# Revit family: toledo_flatliner_901631_002_76_a09a
name_source: partatom
category: Lighting Fixtures
units: mm (PartAtom-declared; Revit-internal decimal feet)

## family parameters
Cut with Voids When Loaded = No
Host = Face
Light Source = No
Part Type = Normal
Room Calculation Point = No
Round Connector Dimension = Use Diameter
Shared = No

## types (1)
- 982300.002 (1 x LED Modul 830, 610 lm, 3000)
    Apparent Load = 8 VA
    CIE Flux Codes = 56 78 92 81 100
    Color Rendering = 80
    Color Temperature = 3000
    Default Elevation = 1800 mm
    Description = Series: TOLEDO FLATLINER
Decorative pendant luminaire for interior decoration. Base luminaire prepared for the installation of fabric lampshade. Cylinder housing sheet steel, powder-coated. Housing: die cast aluminium and sheet steel, powder-coated. Bezel ring: die-cast aluminium, powder-coated. Canopy: sheet steel, powder-coated. Lightguide and diffuser made of non-yellowing plastic (PMMA) opal matt. Transparent suspension cable 2 m, can be shortened. Modular design: With the basic luminaire, a square or cylindrical fabric lampshade must always be ordered separately. Fabric lampshades can be fitted to the basic luminaire without tools. Order satin finish diffuser as separate accessory. 
Colour: white
Diameter: 204 mm
Height: 90.5 mm
Suspension length: 2000 mm
Lamp: LED
Socket: without socket
Colour temperature: 3000K
Colour rendering index (CRI): 80
System power: 7.7 W
Rated luminous flux: 610 lm
Luminous efficiency: 79 lm/W
Control gear: Converter, dimmable, DALI
Protection class: I
Type of protection: IP 20
    Height = 91 mm
    Lamp = 1 x LED Modul 830
    Lamp Light Flux = 610 lm
    Lamp count = 1
    Length = 204 mm
    Lifetime = 50000 h
    Luminous efficacy = 79 lm/W
    Manufacturer = RZB
    ModVariant = No
    Model = 901631.002.76
    Mounting Place = Ceiling
    Mounting Type = Pendant
    Number of Poles = 1
    OnlyDefault = Yes
    Power Factor = 1
    Product Name = TOLEDO FLATLINER
    Product group = Pendant-Fabric lampshade luminaires
    ProductGroupID = 913
    Protection Class = Protection class I
    Protection Degree = IP 20
    RLX_Detail_Level = 1
    RLX_Emergency_Light_Flux = 0 lm
    RLX_Emergency_Type = 0
    RLX_Emergency_Type_DB = No
    RlxData = <blob elided: 48449 chars, md5=f884ae04>
    Socket = socket
    Standby Power = 0 W
    System Light Flux = 610 lm
    System Power = 8 W
    Type Image = toledo_flatliner_pendel_runde_grun_odeckel.jpg
    URL = http://relux.com
    VarID = 982300_002_5a54
    Voltage = 230 V
    Voltage Range = 220-240 V
    Weight = 0.00 kg
    Width = 0 mm  [stored 0 ft]

note: [stored X ft] marks values corroborated as IEEE doubles in the binary element streams (Revit-internal decimal feet)

## geometry (parser evidence)
native form markers: Sweep x11
no freeform markers — native parametric forms only
